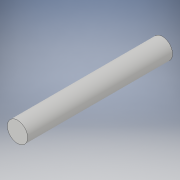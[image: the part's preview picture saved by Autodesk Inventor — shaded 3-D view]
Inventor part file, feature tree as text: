
AUTODESK INVENTOR PART (.ipt)
format: ipt  version: 2019 (Build 230136000, 136)  size: 90,624 bytes
history: native  units: mm
features: extrude x1, sketch x1
ambient origin geometry x8: Origin, YZ Plane, XZ Plane, XY Plane, X Axis, Y Axis, Z Axis, Center Point
bodies: Solid1 (feature_tree)
feature tree (2):
  extrude  "Extrusion1"  Depth=50.0mm TaperAngle=0.0deg
  sketch  "Sketch1"  dims[d0=7.0mm d1=50.0mm d2=0.0mm]
